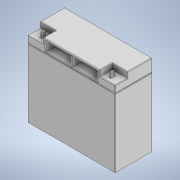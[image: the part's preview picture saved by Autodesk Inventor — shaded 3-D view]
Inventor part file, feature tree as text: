
AUTODESK INVENTOR PART (.ipt)
format: ipt  version: 2020 (Build 240168000, 168)  size: 211,968 bytes
history: native  units: in
note: dims shown in document units (in); Inventor stores cm internally (conversion verified against a paired STEP export)
features: other x1, fillet x1
ambient origin geometry x8: Origin, YZ Plane, XZ Plane, XY Plane, X Axis, Y Axis, Z Axis, Center Point
bodies: Solid1 (feature_tree)
feature tree (2):
  other  "Battery.STEP"
  fillet  "Fillet4"  [1 undecoded]
note: 1 required parameter value undecoded (feature->parameter linkage not recoverable at this tier; creation-order binding heuristic only, values carry confidence <= 0.55)
